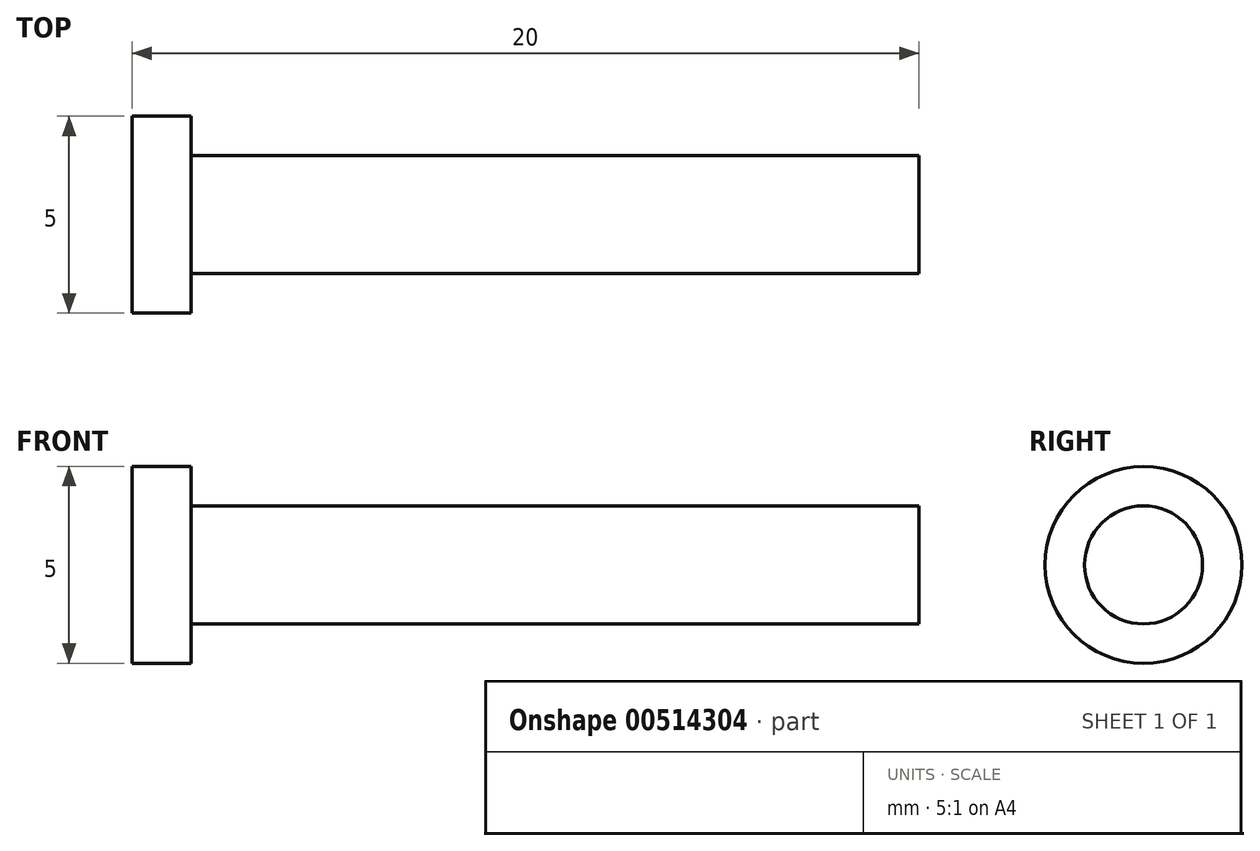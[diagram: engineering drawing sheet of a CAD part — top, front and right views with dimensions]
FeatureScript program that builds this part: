
annotation { "Feature Type Name" : "Feature", "Feature Type Description" : "" }
export const myFeature = defineFeature(function(context is Context, id is Id, definition is map)
    precondition{}
    {
        {
            var Q0;
            Q0=qCreatedBy(makeId("Top.planeOp"),FACE);
            var sketch = newSketch(context, id + "F0", { "sketchPlane" : qUnion([Q0])});
            skLineSegment(sketch, "E0", {"start": v(-67.75, 0) * mm, "end": v(79.1, 0) * mm, "construction": true});
            skLineSegment(sketch, "E1", {"start": v(-1.5, 0) * mm, "end": v(-1.5, 2.5) * mm});
            skLineSegment(sketch, "E2", {"start": v(-1.5, 2.5) * mm, "end": v(0, 2.5) * mm});
            skLineSegment(sketch, "E3", {"start": v(0, 2.5) * mm, "end": v(0, 1.5) * mm});
            skLineSegment(sketch, "E4", {"start": v(0, 1.5) * mm, "end": v(18.5, 1.5) * mm});
            skLineSegment(sketch, "E5", {"start": v(18.5, 1.5) * mm, "end": v(18.5, 0) * mm});
            skLineSegment(sketch, "E6", {"start": v(18.5, 0) * mm, "end": v(-1.5, 0) * mm});
            skSolve(sketch);
        }
        {
            var Q0;
            Q0 = qSketchRegion(id + "F0", true);
            var Q1;
            Q1=sQuery(id+"F0.wireOp",EDGE,"E6");
            revolve(context, id + "F1", {"entities" : qUnion([Q0]), "axis" : qUnion([Q1]), "revolveType" : RevolveType.FULL});
        }
    });
